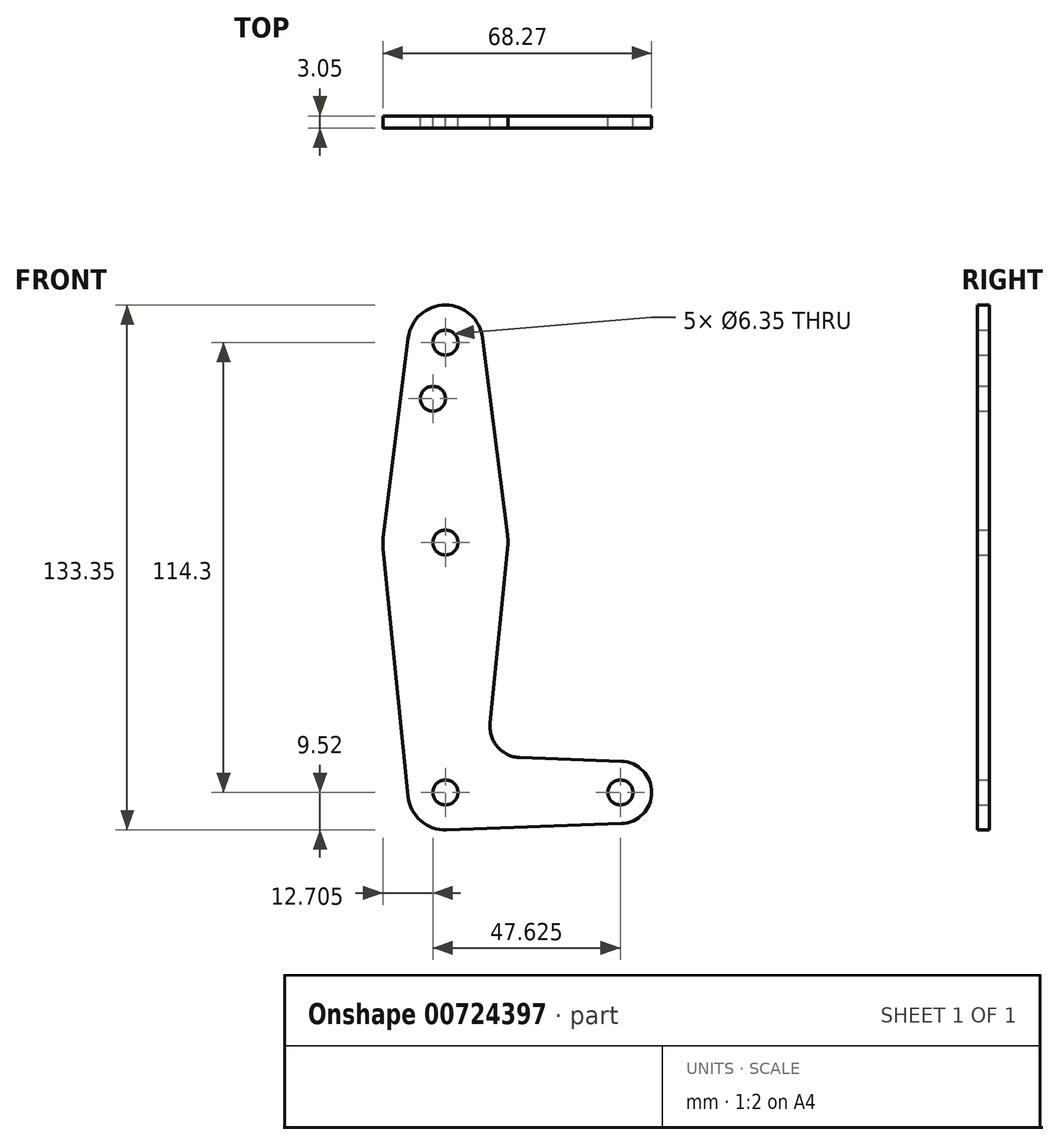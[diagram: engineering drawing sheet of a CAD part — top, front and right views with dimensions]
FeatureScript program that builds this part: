
annotation { "Feature Type Name" : "Feature", "Feature Type Description" : "" }
export const myFeature = defineFeature(function(context is Context, id is Id, definition is map)
    precondition{}
    {
        {
            var Q0;
            Q0=qCreatedBy(makeId("Front.planeOp"),FACE);
            var sketch = newSketch(context, id + "F0", { "sketchPlane" : qUnion([Q0])});
            skLineSegment(sketch, "E0", {"start": v(0, 114.3) * mm, "end": v(0, 0) * mm, "construction": true});
            skLineSegment(sketch, "E1", {"start": v(0, 0) * mm, "end": v(44.45, 0) * mm, "construction": true});
            skCircle(sketch, "E2", {"center": v(0, 114.3) * mm, "radius": 9.53 * mm});
            skCircle(sketch, "E3", {"center": v(0, 0) * mm, "radius": 9.53 * mm});
            skCircle(sketch, "E4", {"center": v(44.45, 0) * mm, "radius": 7.94 * mm});
            skCircle(sketch, "E5", {"center": v(0, 63.5) * mm, "radius": 15.88 * mm});
            skLineSegment(sketch, "E6", {"start": v(-9.45, 115.5) * mm, "end": v(-15.75, 65.48) * mm});
            skLineSegment(sketch, "E7", {"start": v(9.45, 115.5) * mm, "end": v(15.75, 65.48) * mm});
            skLineSegment(sketch, "E8", {"start": v(15.8, 61.91) * mm, "end": v(11.34, 17.6) * mm});
            skLineSegment(sketch, "E9", {"start": v(-15.8, 61.91) * mm, "end": v(-9.48, -0.95) * mm});
            skLineSegment(sketch, "E10", {"start": v(18.97, 8.85) * mm, "end": v(44.73, 7.93) * mm});
            skLineSegment(sketch, "E11", {"start": v(0.34, -9.52) * mm, "end": v(44.73, -7.93) * mm});
            skCircle(sketch, "E12", {"center": v(44.45, 0) * mm, "radius": 3.18 * mm});
            skCircle(sketch, "E13", {"center": v(0, 0) * mm, "radius": 3.18 * mm});
            skCircle(sketch, "E14", {"center": v(0, 63.5) * mm, "radius": 3.18 * mm});
            skCircle(sketch, "E15", {"center": v(0, 114.3) * mm, "radius": 3.18 * mm});
            skCircle(sketch, "E16", {"center": v(-3.17, 100.03) * mm, "radius": 3.18 * mm});
            skArc(sketch, "E17.filletArc", {"start": v(11.34, 17.6) * mm, "mid": v(13.26, 11.57) * mm, "end": v(18.97, 8.85) * mm});
            skSolve(sketch);
        }
        {
            var Q0;
            Q0 = qSketchRegion(id + "F0", true);
            extrude(context, id + "F1", {"entities" : qUnion([Q0]), "depth" : 3.05 * mm, "offsetDistance" : 25.4 * mm});
        }
    });
